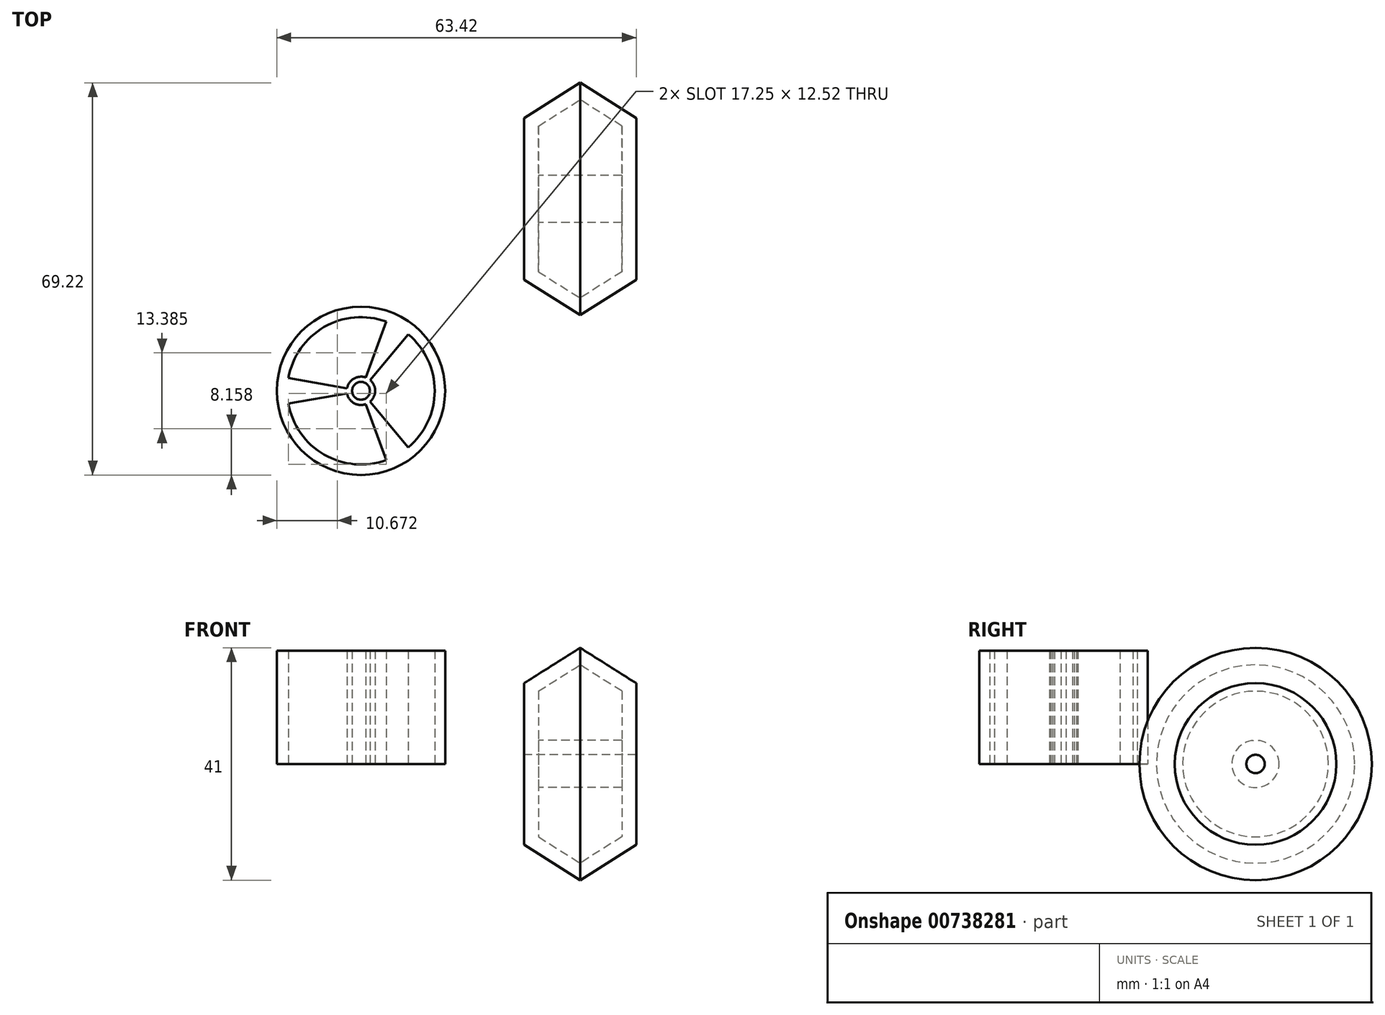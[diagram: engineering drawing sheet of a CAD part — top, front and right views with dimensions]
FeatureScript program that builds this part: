
annotation { "Feature Type Name" : "Feature", "Feature Type Description" : "" }
export const myFeature = defineFeature(function(context is Context, id is Id, definition is map)
    precondition{}
    {
        {
            var Q0;
            Q0=qCreatedBy(makeId("Top.planeOp"),FACE);
            var sketch = newSketch(context, id + "F0", { "sketchPlane" : qUnion([Q0])});
            skCircle(sketch, "E0", {"center": v(0, 0) * mm, "radius": 14.85 * mm});
            skCircle(sketch, "E1", {"center": v(0, 0) * mm, "radius": 1.57 * mm});
            skCircle(sketch, "E2", {"center": v(0, 0) * mm, "radius": 13 * mm});
            skLineSegment(sketch, "E3", {"start": v(0, 0) * mm, "end": v(5.08, -13.95) * mm});
            skLineSegment(sketch, "E4", {"start": v(0, 0) * mm, "end": v(9.55, -11.38) * mm});
            skLineSegment(sketch, "E5", {"start": v(0, 0) * mm, "end": v(-14.62, -2.58) * mm});
            skLineSegment(sketch, "E6", {"start": v(0, 0) * mm, "end": v(-14.62, 2.58) * mm});
            skLineSegment(sketch, "E7", {"start": v(0, 0) * mm, "end": v(5.08, 13.95) * mm});
            skLineSegment(sketch, "E8", {"start": v(0, 0) * mm, "end": v(9.55, 11.38) * mm});
            skCircle(sketch, "E9", {"center": v(0, 0) * mm, "radius": 2.5 * mm});
            skSolve(sketch);
        }
        {
            var Q0;
            {var subQ0=sQuery(id+"F0.wireOp",EDGE,"E3");var subQ1=sQuery(id+"F0.wireOp",EDGE,"E0");var subQ2=makeQuery(id+"F0.imprint","INTERSECT",VERTEX,{"derivedFrom":[subQ1,subQ0]});Q0=makeQuery(id+"F0.imprint","IMPRINT",FACE,{"disambiguationData":[TD([[makeQuery(id+"F0.imprint","IMPRINT",EDGE,{"disambiguationData":[TD([[subQ2,1.0]])],"derivedFrom":subQ1}),1.0]])]});}
            var Q1;
            {var subQ0=sQuery(id+"F0.wireOp",EDGE,"E5");var subQ1=sQuery(id+"F0.wireOp",EDGE,"E0");var subQ2=makeQuery(id+"F0.imprint","INTERSECT",VERTEX,{"derivedFrom":[subQ1,subQ0]});Q1=makeQuery(id+"F0.imprint","IMPRINT",FACE,{"disambiguationData":[TD([[makeQuery(id+"F0.imprint","IMPRINT",EDGE,{"disambiguationData":[TD([[subQ2,1.0]])],"derivedFrom":subQ1}),1.0]])]});}
            var Q2;
            {var subQ0=sQuery(id+"F0.wireOp",EDGE,"E6");var subQ1=sQuery(id+"F0.wireOp",EDGE,"E2");var subQ2=makeQuery(id+"F0.imprint","INTERSECT",VERTEX,{"derivedFrom":[subQ1,subQ0]});Q2=makeQuery(id+"F0.imprint","IMPRINT",FACE,{"disambiguationData":[TD([[makeQuery(id+"F0.imprint","IMPRINT",EDGE,{"disambiguationData":[TD([[subQ2,-1.0]])],"derivedFrom":subQ1}),1.0]])]});}
            var Q3;
            {var subQ0=sQuery(id+"F0.wireOp",EDGE,"E6");var subQ1=sQuery(id+"F0.wireOp",EDGE,"E0");var subQ2=makeQuery(id+"F0.imprint","INTERSECT",VERTEX,{"derivedFrom":[subQ1,subQ0]});Q3=makeQuery(id+"F0.imprint","IMPRINT",FACE,{"disambiguationData":[TD([[makeQuery(id+"F0.imprint","IMPRINT",EDGE,{"disambiguationData":[TD([[subQ2,1.0]])],"derivedFrom":subQ1}),1.0]])]});}
            var Q4;
            {var subQ0=sQuery(id+"F0.wireOp",EDGE,"E5");var subQ1=sQuery(id+"F0.wireOp",EDGE,"E1");var subQ2=makeQuery(id+"F0.imprint","INTERSECT",VERTEX,{"derivedFrom":[subQ1,subQ0]});Q4=makeQuery(id+"F0.imprint","IMPRINT",FACE,{"disambiguationData":[TD([[makeQuery(id+"F0.imprint","IMPRINT",EDGE,{"disambiguationData":[TD([[subQ2,-1.0]])],"derivedFrom":subQ1}),-1.0]])]});}
            var Q5;
            {var subQ0=sQuery(id+"F0.wireOp",EDGE,"E8");var subQ1=sQuery(id+"F0.wireOp",EDGE,"E1");var subQ2=makeQuery(id+"F0.imprint","INTERSECT",VERTEX,{"derivedFrom":[subQ1,subQ0]});Q5=makeQuery(id+"F0.imprint","IMPRINT",FACE,{"disambiguationData":[TD([[makeQuery(id+"F0.imprint","IMPRINT",EDGE,{"disambiguationData":[TD([[subQ2,1.0]])],"derivedFrom":subQ1}),-1.0]])]});}
            var Q6;
            {var subQ0=sQuery(id+"F0.wireOp",EDGE,"E7");var subQ1=sQuery(id+"F0.wireOp",EDGE,"E1");var subQ2=makeQuery(id+"F0.imprint","INTERSECT",VERTEX,{"derivedFrom":[subQ1,subQ0]});Q6=makeQuery(id+"F0.imprint","IMPRINT",FACE,{"disambiguationData":[TD([[makeQuery(id+"F0.imprint","IMPRINT",EDGE,{"disambiguationData":[TD([[subQ2,-1.0]])],"derivedFrom":subQ1}),-1.0]])]});}
            var Q7;
            {var subQ0=sQuery(id+"F0.wireOp",EDGE,"E6");var subQ1=sQuery(id+"F0.wireOp",EDGE,"E1");var subQ2=makeQuery(id+"F0.imprint","INTERSECT",VERTEX,{"derivedFrom":[subQ1,subQ0]});Q7=makeQuery(id+"F0.imprint","IMPRINT",FACE,{"disambiguationData":[TD([[makeQuery(id+"F0.imprint","IMPRINT",EDGE,{"disambiguationData":[TD([[subQ2,-1.0]])],"derivedFrom":subQ1}),-1.0]])]});}
            var Q8;
            {var subQ0=sQuery(id+"F0.wireOp",EDGE,"E7");var subQ1=sQuery(id+"F0.wireOp",EDGE,"E1");var subQ2=makeQuery(id+"F0.imprint","INTERSECT",VERTEX,{"derivedFrom":[subQ1,subQ0]});Q8=makeQuery(id+"F0.imprint","IMPRINT",FACE,{"disambiguationData":[TD([[makeQuery(id+"F0.imprint","IMPRINT",EDGE,{"disambiguationData":[TD([[subQ2,1.0]])],"derivedFrom":subQ1}),-1.0]])]});}
            var Q9;
            {var subQ0=sQuery(id+"F0.wireOp",EDGE,"E3");var subQ1=sQuery(id+"F0.wireOp",EDGE,"E1");var subQ2=makeQuery(id+"F0.imprint","INTERSECT",VERTEX,{"derivedFrom":[subQ1,subQ0]});Q9=makeQuery(id+"F0.imprint","IMPRINT",FACE,{"disambiguationData":[TD([[makeQuery(id+"F0.imprint","IMPRINT",EDGE,{"disambiguationData":[TD([[subQ2,-1.0]])],"derivedFrom":subQ1}),-1.0]])]});}
            var Q10;
            {var subQ0=sQuery(id+"F0.wireOp",EDGE,"E3");var subQ1=sQuery(id+"F0.wireOp",EDGE,"E2");var subQ2=makeQuery(id+"F0.imprint","INTERSECT",VERTEX,{"derivedFrom":[subQ1,subQ0]});Q10=makeQuery(id+"F0.imprint","IMPRINT",FACE,{"disambiguationData":[TD([[makeQuery(id+"F0.imprint","IMPRINT",EDGE,{"disambiguationData":[TD([[subQ2,-1.0]])],"derivedFrom":subQ1}),1.0]])]});}
            var Q11;
            {var subQ0=sQuery(id+"F0.wireOp",EDGE,"E7");var subQ1=sQuery(id+"F0.wireOp",EDGE,"E2");var subQ2=makeQuery(id+"F0.imprint","INTERSECT",VERTEX,{"derivedFrom":[subQ1,subQ0]});Q11=makeQuery(id+"F0.imprint","IMPRINT",FACE,{"disambiguationData":[TD([[makeQuery(id+"F0.imprint","IMPRINT",EDGE,{"disambiguationData":[TD([[subQ2,1.0]])],"derivedFrom":subQ1}),1.0]])]});}
            var Q12;
            {var subQ0=sQuery(id+"F0.wireOp",EDGE,"E4");var subQ1=sQuery(id+"F0.wireOp",EDGE,"E0");var subQ2=makeQuery(id+"F0.imprint","INTERSECT",VERTEX,{"derivedFrom":[subQ1,subQ0]});Q12=makeQuery(id+"F0.imprint","IMPRINT",FACE,{"disambiguationData":[TD([[makeQuery(id+"F0.imprint","IMPRINT",EDGE,{"disambiguationData":[TD([[subQ2,-1.0]])],"derivedFrom":subQ1}),1.0]])]});}
            var Q13;
            {var subQ0=sQuery(id+"F0.wireOp",EDGE,"E3");var subQ1=sQuery(id+"F0.wireOp",EDGE,"E0");var subQ2=makeQuery(id+"F0.imprint","INTERSECT",VERTEX,{"derivedFrom":[subQ1,subQ0]});Q13=makeQuery(id+"F0.imprint","IMPRINT",FACE,{"disambiguationData":[TD([[makeQuery(id+"F0.imprint","IMPRINT",EDGE,{"disambiguationData":[TD([[subQ2,-1.0]])],"derivedFrom":subQ1}),1.0]])]});}
            var Q14;
            {var subQ0=sQuery(id+"F0.wireOp",EDGE,"E7");var subQ1=sQuery(id+"F0.wireOp",EDGE,"E0");var subQ2=makeQuery(id+"F0.imprint","INTERSECT",VERTEX,{"derivedFrom":[subQ1,subQ0]});Q14=makeQuery(id+"F0.imprint","IMPRINT",FACE,{"disambiguationData":[TD([[makeQuery(id+"F0.imprint","IMPRINT",EDGE,{"disambiguationData":[TD([[subQ2,1.0]])],"derivedFrom":subQ1}),1.0]])]});}
            extrude(context, id + "F1", {"entities" : qUnion([Q0, Q1, Q2, Q3, Q4, Q5, Q6, Q7, Q8, Q9, Q10, Q11, Q12, Q13, Q14]), "depth" : 20 * mm, "offsetDistance" : 25.4 * mm});
        }
        {
            var Q0;
            Q0=qCreatedBy(makeId("Top.planeOp"),FACE);
            var sketch = newSketch(context, id + "F2", { "sketchPlane" : qUnion([Q0])});
            skLineSegment(sketch, "E10", {"start": v(48.57, 32.25) * mm, "end": v(28.77, 32.25) * mm});
            skLineSegment(sketch, "E11", {"start": v(28.77, 32.25) * mm, "end": v(28.77, 19.62) * mm});
            skLineSegment(sketch, "E12", {"start": v(28.77, 19.62) * mm, "end": v(38.67, 13.37) * mm});
            skLineSegment(sketch, "E13", {"start": v(38.67, 13.37) * mm, "end": v(48.57, 19.62) * mm});
            skLineSegment(sketch, "E14", {"start": v(48.57, 19.62) * mm, "end": v(48.57, 32.25) * mm});
            skLineSegment(sketch, "E15", {"start": v(25.38, 33.87) * mm, "end": v(61.02, 33.87) * mm});
            skLineSegment(sketch, "E16", {"start": v(31.3, 29.7) * mm, "end": v(31.3, 21.02) * mm});
            skLineSegment(sketch, "E17", {"start": v(31.3, 21.02) * mm, "end": v(38.67, 16.38) * mm});
            skLineSegment(sketch, "E18", {"start": v(38.67, 16.38) * mm, "end": v(46.03, 21.02) * mm});
            skLineSegment(sketch, "E19", {"start": v(46.03, 21.02) * mm, "end": v(46.03, 29.7) * mm});
            skLineSegment(sketch, "E20", {"start": v(31.3, 29.7) * mm, "end": v(46.03, 29.7) * mm});
            skSolve(sketch);
        }
        {
            var Q0;
            Q0=makeQuery(id+"F2.imprint","IMPRINT",FACE,{"disambiguationData":[TD([[makeQuery(id+"F2.imprint","IMPRINT",EDGE,{"derivedFrom":sQuery(id+"F2.wireOp",EDGE,"E10")}),1.0]])]});
            var Q1;
            Q1=sQuery(id+"F2.wireOp",EDGE,"E15");
            revolve(context, id + "F3", {"surfaceOperationType" : NewSurfaceOperationType.NEW, "entities" : qUnion([Q0]), "axis" : qUnion([Q1]), "revolveType" : RevolveType.FULL});
        }
    });
